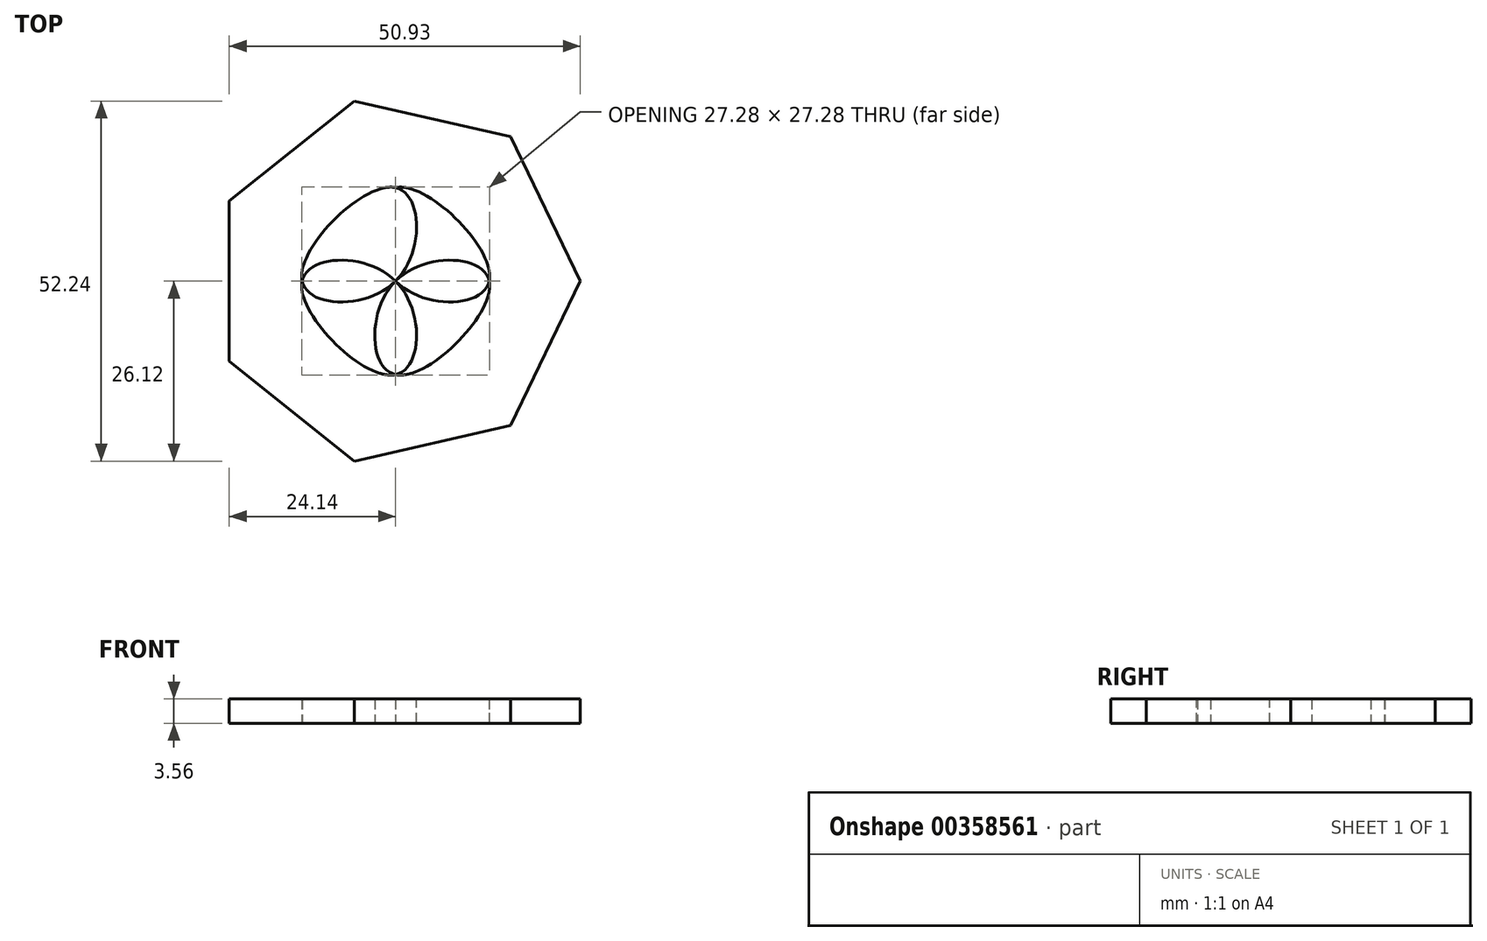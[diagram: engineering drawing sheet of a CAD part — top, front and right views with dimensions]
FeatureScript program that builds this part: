
annotation { "Feature Type Name" : "Feature", "Feature Type Description" : "" }
export const myFeature = defineFeature(function(context is Context, id is Id, definition is map)
    precondition{}
    {
        {
            var Q0;
            Q0=qCreatedBy(makeId("Top.planeOp"),FACE);
            var sketch = newSketch(context, id + "F0", { "sketchPlane" : qUnion([Q0])});
            skCircle(sketch, "E0.cCircle", {"center": v(0, 0) * mm, "radius": 24.14 * mm, "construction": true});
            skLineSegment(sketch, "E0.0", {"start": v(-24.14, -11.62) * mm, "end": v(-24.14, 11.62) * mm});
            skLineSegment(sketch, "E0.1", {"start": v(-24.14, 11.62) * mm, "end": v(-5.96, 26.12) * mm});
            skLineSegment(sketch, "E0.2", {"start": v(-5.96, 26.12) * mm, "end": v(16.7, 20.95) * mm});
            skLineSegment(sketch, "E0.3", {"start": v(16.7, 20.95) * mm, "end": v(26.8, 0) * mm});
            skLineSegment(sketch, "E0.4", {"start": v(26.8, 0) * mm, "end": v(16.7, -20.95) * mm});
            skLineSegment(sketch, "E0.5", {"start": v(16.7, -20.95) * mm, "end": v(-5.96, -26.12) * mm});
            skLineSegment(sketch, "E0.6", {"start": v(-5.96, -26.12) * mm, "end": v(-24.14, -11.62) * mm});
            skPoint(sketch, "E0.0.midPoint", {"position": v(-24.14, 0) * mm});
            skCircle(sketch, "E1", {"center": v(0, 0) * mm, "radius": 13.57 * mm});
            skFitSpline(sketch, "E2", {"points": [v(0, 0) * mm, v(13.57, 0) * mm, v(0, 13.57) * mm, v(0, 0) * mm]});
            skFitSpline(sketch, "E3", {"points": [v(-13.57, 0) * mm, v(0, 13.57) * mm, v(0, 0) * mm, v(-13.57, 0) * mm]});
            skFitSpline(sketch, "E4", {"points": [v(-13.57, 0) * mm, v(0, 0) * mm, v(0, -13.57) * mm, v(-13.57, 0) * mm]});
            skFitSpline(sketch, "E5", {"points": [v(0, 0) * mm, v(0, -13.57) * mm, v(13.57, 0) * mm, v(0, 0) * mm]});
            skSolve(sketch);
        }
        {
            var Q0;
            {var subQ0=sQuery(id+"F0.wireOp",EDGE,"E5");var subQ1=sQuery(id+"F0.wireOp",EDGE,"E3");var subQ2=makeQuery(id+"F0.imprint","INTERSECT",VERTEX,{"derivedFrom":[subQ1,subQ0]});Q0=makeQuery(id+"F0.imprint","IMPRINT",FACE,{"disambiguationData":[TD([[makeQuery(id+"F0.imprint","IMPRINT",EDGE,{"disambiguationData":[TD([[subQ2,-1.0]])],"derivedFrom":subQ1}),-1.0]])]});}
            var Q1;
            Q1=makeQuery(id+"F0.imprint","IMPRINT",FACE,{"disambiguationData":[TD([[makeQuery(id+"F0.imprint","IMPRINT",EDGE,{"derivedFrom":sQuery(id+"F0.wireOp",EDGE,"E0.0")}),-1.0]])]});
            var Q2;
            {var subQ0=sQuery(id+"F0.wireOp",EDGE,"E3");var subQ1=sQuery(id+"F0.wireOp",EDGE,"E2");var subQ2=makeQuery(id+"F0.imprint","INTERSECT",VERTEX,{"derivedFrom":[sQuery(id+"F0.wireOp",EDGE,"E1"),subQ1,subQ0]});Q2=makeQuery(id+"F0.imprint","IMPRINT",FACE,{"disambiguationData":[TD([[makeQuery(id+"F0.imprint","IMPRINT",EDGE,{"disambiguationData":[TD([[subQ2,-1.0]])],"derivedFrom":subQ1}),1.0]])]});}
            var Q3;
            {var subQ0=sQuery(id+"F0.wireOp",EDGE,"E4");var subQ1=sQuery(id+"F0.wireOp",EDGE,"E2");var subQ2=makeQuery(id+"F0.imprint","INTERSECT",VERTEX,{"derivedFrom":[subQ1,subQ0]});Q3=makeQuery(id+"F0.imprint","IMPRINT",FACE,{"disambiguationData":[TD([[makeQuery(id+"F0.imprint","IMPRINT",EDGE,{"disambiguationData":[TD([[subQ2,-1.0]])],"derivedFrom":subQ1}),1.0]])]});}
            var Q4;
            {var subQ0=sQuery(id+"F0.wireOp",EDGE,"E4");var subQ1=sQuery(id+"F0.wireOp",EDGE,"E2");var subQ2=makeQuery(id+"F0.imprint","INTERSECT",VERTEX,{"derivedFrom":[subQ1,subQ0]});Q4=makeQuery(id+"F0.imprint","IMPRINT",FACE,{"disambiguationData":[TD([[makeQuery(id+"F0.imprint","IMPRINT",EDGE,{"disambiguationData":[TD([[subQ2,-1.0]])],"derivedFrom":subQ0}),-1.0]])]});}
            var Q5;
            {var subQ0=sQuery(id+"F0.wireOp",EDGE,"E4");var subQ1=sQuery(id+"F0.wireOp",EDGE,"E1");var subQ2=makeQuery(id+"F0.imprint","INTERSECT",VERTEX,{"disambiguationData":[OD(0.0)],"derivedFrom":[subQ1,subQ0]});Q5=makeQuery(id+"F0.imprint","IMPRINT",FACE,{"disambiguationData":[TD([[makeQuery(id+"F0.imprint","IMPRINT",EDGE,{"disambiguationData":[TD([[subQ2,-1.0]])],"derivedFrom":subQ1}),1.0]])]});}
            var Q6;
            {var subQ0=sQuery(id+"F0.wireOp",EDGE,"E3");var subQ1=sQuery(id+"F0.wireOp",EDGE,"E1");var subQ2=makeQuery(id+"F0.imprint","INTERSECT",VERTEX,{"disambiguationData":[OD(0.0)],"derivedFrom":[subQ1,subQ0]});Q6=makeQuery(id+"F0.imprint","IMPRINT",FACE,{"disambiguationData":[TD([[makeQuery(id+"F0.imprint","IMPRINT",EDGE,{"disambiguationData":[TD([[subQ2,-1.0]])],"derivedFrom":subQ1}),1.0]])]});}
            var Q7;
            {var subQ0=sQuery(id+"F0.wireOp",EDGE,"E2");var subQ1=sQuery(id+"F0.wireOp",EDGE,"E1");var subQ2=makeQuery(id+"F0.imprint","INTERSECT",VERTEX,{"disambiguationData":[OD(0.0)],"derivedFrom":[subQ1,subQ0]});Q7=makeQuery(id+"F0.imprint","IMPRINT",FACE,{"disambiguationData":[TD([[makeQuery(id+"F0.imprint","IMPRINT",EDGE,{"disambiguationData":[TD([[subQ2,-1.0]])],"derivedFrom":subQ1}),1.0]])]});}
            var Q8;
            {var subQ0=sQuery(id+"F0.wireOp",EDGE,"E5");var subQ1=sQuery(id+"F0.wireOp",EDGE,"E1");var subQ2=makeQuery(id+"F0.imprint","INTERSECT",VERTEX,{"disambiguationData":[OD(0.0)],"derivedFrom":[subQ1,subQ0]});Q8=makeQuery(id+"F0.imprint","IMPRINT",FACE,{"disambiguationData":[TD([[makeQuery(id+"F0.imprint","IMPRINT",EDGE,{"disambiguationData":[TD([[subQ2,-1.0]])],"derivedFrom":subQ1}),1.0]])]});}
            extrude(context, id + "F1", {"entities" : qUnion([Q0, Q1, Q2, Q3, Q4, Q5, Q6, Q7, Q8]), "depth" : 3.56 * mm});
        }
    });
